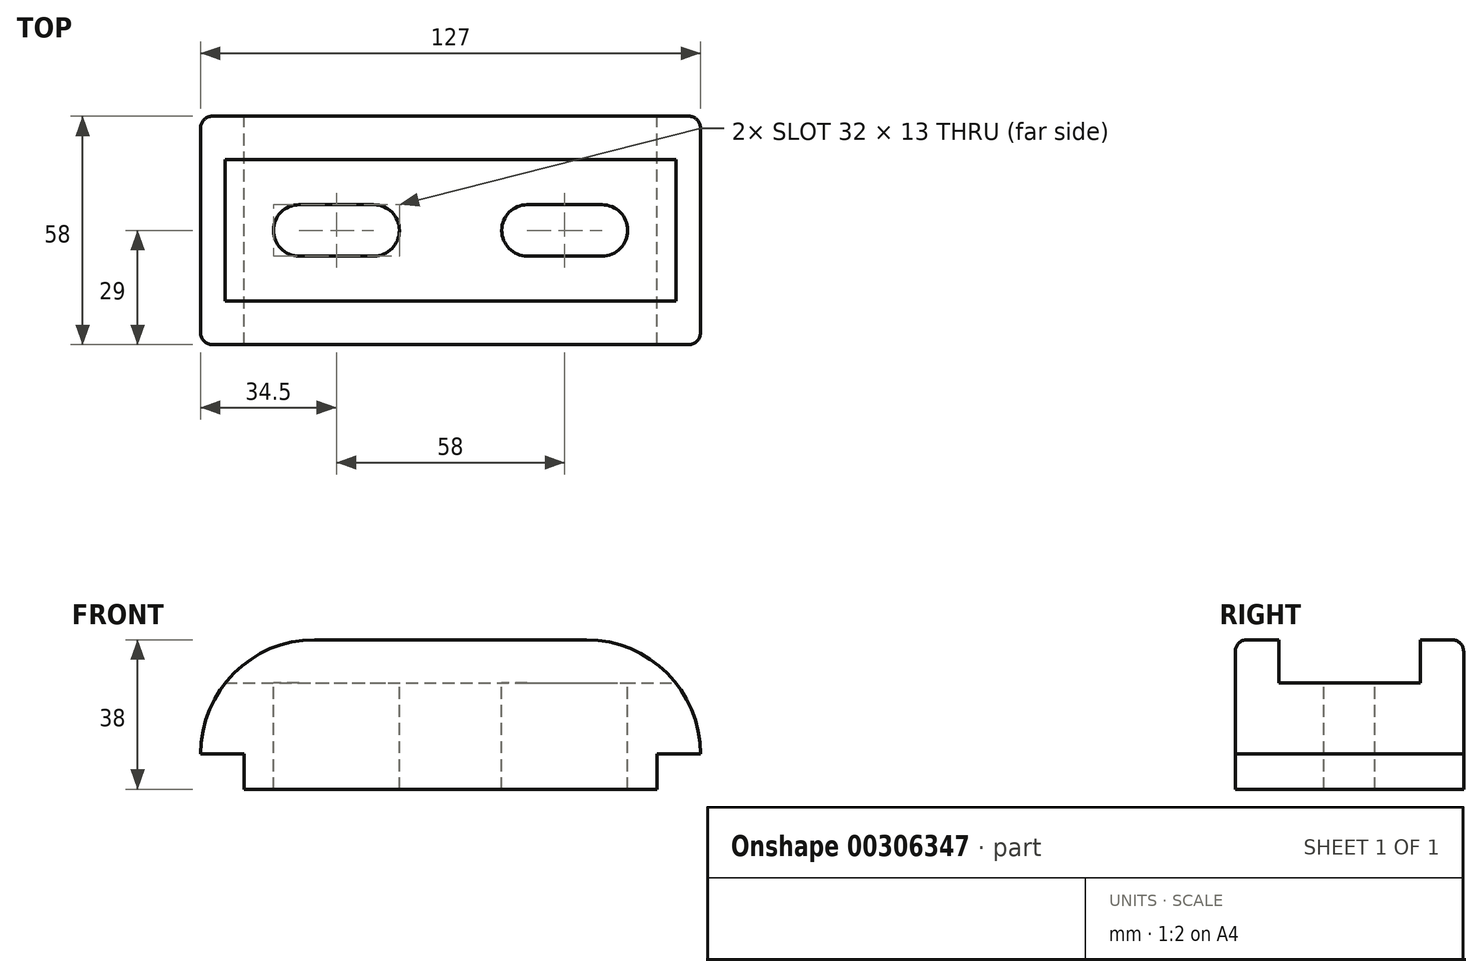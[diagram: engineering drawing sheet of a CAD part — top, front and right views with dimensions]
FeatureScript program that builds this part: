
annotation { "Feature Type Name" : "Feature", "Feature Type Description" : "" }
export const myFeature = defineFeature(function(context is Context, id is Id, definition is map)
    precondition{}
    {
        {
            var Q0;
            Q0=qCreatedBy(makeId("Front.planeOp"),FACE);
            var sketch = newSketch(context, id + "F0", { "sketchPlane" : qUnion([Q0])});
            skLineSegment(sketch, "E0", {"start": v(0, 0) * mm, "end": v(0, 9) * mm});
            skLineSegment(sketch, "E1", {"start": v(0, 9) * mm, "end": v(-11, 9) * mm});
            skLineSegment(sketch, "E2", {"start": v(0, 0) * mm, "end": v(105, 0) * mm});
            skLineSegment(sketch, "E3", {"start": v(105, 0) * mm, "end": v(105, 9) * mm});
            skLineSegment(sketch, "E4", {"start": v(105, 9) * mm, "end": v(116, 9) * mm});
            skLineSegment(sketch, "E5", {"start": v(18, 38) * mm, "end": v(87, 38) * mm});
            skArc(sketch, "E6", {"start": v(116, 9) * mm, "mid": v(107.5, 29.5) * mm, "end": v(87, 38) * mm});
            skArc(sketch, "E7", {"start": v(18, 38) * mm, "mid": v(-2.5, 29.5) * mm, "end": v(-11, 9) * mm});
            skSolve(sketch);
        }
        {
            var Q0;
            Q0 = qSketchRegion(id + "F0", true);
            extrude(context, id + "F1", {"entities" : qUnion([Q0]), "depth" : 58 * mm});
        }
        {
            var Q0;
            Q0=makeQuery(id+"F1.opExtrude","SWEPT_FACE",FACE,{"disambiguationData":[OSD([sQuery(id+"F0.wireOp",EDGE,"E5")])]});
            var sketch = newSketch(context, id + "F2", { "sketchPlane" : qUnion([Q0])});
            skLineSegment(sketch, "E8.bottom", {"start": v(-11, -11) * mm, "end": v(116, -11) * mm});
            skLineSegment(sketch, "E8.top", {"start": v(-11, -47) * mm, "end": v(116, -47) * mm});
            skLineSegment(sketch, "E8.left", {"start": v(-11, -11) * mm, "end": v(-11, -47) * mm});
            skLineSegment(sketch, "E8.right", {"start": v(116, -11) * mm, "end": v(116, -47) * mm});
            skSolve(sketch);
        }
        {
            var Q0;
            Q0 = qSketchRegion(id + "F2", true);
            extrude(context, id + "F3", {"entities" : qUnion([Q0]), "operationType" : NewBodyOperationType.REMOVE, "oppositeDirection" : true, "depth" : 11 * mm});
        }
        {
            var Q0;
            Q0=makeQuery(id+"F3.boolean.opBoolean","COPY",FACE,{"derivedFrom":makeQuery(id+"F3.opExtrude","CAP_FACE",FACE,{"disambiguationData":[OSD([sQuery(id+"F2.wireOp",EDGE,"E8.bottom"),sQuery(id+"F2.wireOp",EDGE,"E8.top"),sQuery(id+"F2.wireOp",EDGE,"E8.left"),sQuery(id+"F2.wireOp",EDGE,"E8.right")])],"isStart":false})});
            var sketch = newSketch(context, id + "F4", { "sketchPlane" : qUnion([Q0])});
            skArc(sketch, "E9", {"start": v(14, -22.5) * mm, "mid": v(7.5, -29) * mm, "end": v(14, -35.5) * mm});
            skArc(sketch, "E10", {"start": v(33, -35.5) * mm, "mid": v(39.5, -29) * mm, "end": v(33, -22.5) * mm});
            skArc(sketch, "E11", {"start": v(72, -22.5) * mm, "mid": v(65.5, -29) * mm, "end": v(72, -35.5) * mm});
            skArc(sketch, "E12", {"start": v(91, -35.5) * mm, "mid": v(97.5, -29) * mm, "end": v(91, -22.5) * mm});
            skLineSegment(sketch, "E13", {"start": v(14, -22.5) * mm, "end": v(33, -22.5) * mm});
            skLineSegment(sketch, "E14", {"start": v(14, -35.5) * mm, "end": v(33, -35.5) * mm});
            skLineSegment(sketch, "E15", {"start": v(72, -35.5) * mm, "end": v(91, -35.5) * mm});
            skLineSegment(sketch, "E16", {"start": v(72, -22.5) * mm, "end": v(91, -22.5) * mm});
            skSolve(sketch);
        }
        {
            var Q0;
            Q0 = qSketchRegion(id + "F4", true);
            extrude(context, id + "F5", {"entities" : qUnion([Q0]), "operationType" : NewBodyOperationType.REMOVE, "endBound" : BoundingType.THROUGH_ALL, "oppositeDirection" : true, "depth" : 25 * mm});
        }
        {
            var Q0;
            Q0=makeQuery(id+"F1.opExtrude","CAP_EDGE",EDGE,{"disambiguationData":[OSD([sQuery(id+"F0.wireOp",EDGE,"E5")])],"isStart":false});
            var Q1;
            Q1=makeQuery(id+"F1.opExtrude","CAP_EDGE",EDGE,{"disambiguationData":[OSD([sQuery(id+"F0.wireOp",EDGE,"E6")])],"isStart":false});
            var Q2;
            Q2=makeQuery(id+"F1.opExtrude","CAP_EDGE",EDGE,{"disambiguationData":[OSD([sQuery(id+"F0.wireOp",EDGE,"E7")])],"isStart":false});
            var Q3;
            Q3=makeQuery(id+"F1.opExtrude","CAP_EDGE",EDGE,{"disambiguationData":[OSD([sQuery(id+"F0.wireOp",EDGE,"E5")])],"isStart":true});
            var Q4;
            Q4=makeQuery(id+"F1.opExtrude","CAP_EDGE",EDGE,{"disambiguationData":[OSD([sQuery(id+"F0.wireOp",EDGE,"E7")])],"isStart":true});
            var Q5;
            Q5=makeQuery(id+"F1.opExtrude","CAP_EDGE",EDGE,{"disambiguationData":[OSD([sQuery(id+"F0.wireOp",EDGE,"E6")])],"isStart":true});
            fillet(context, id + "F6", {"entities" : qUnion([Q0, Q1, Q2, Q3, Q4, Q5]), "radius" : 3 * mm, "tangentPropagation" : true, "allowEdgeOverflow" : false});
        }
    });
